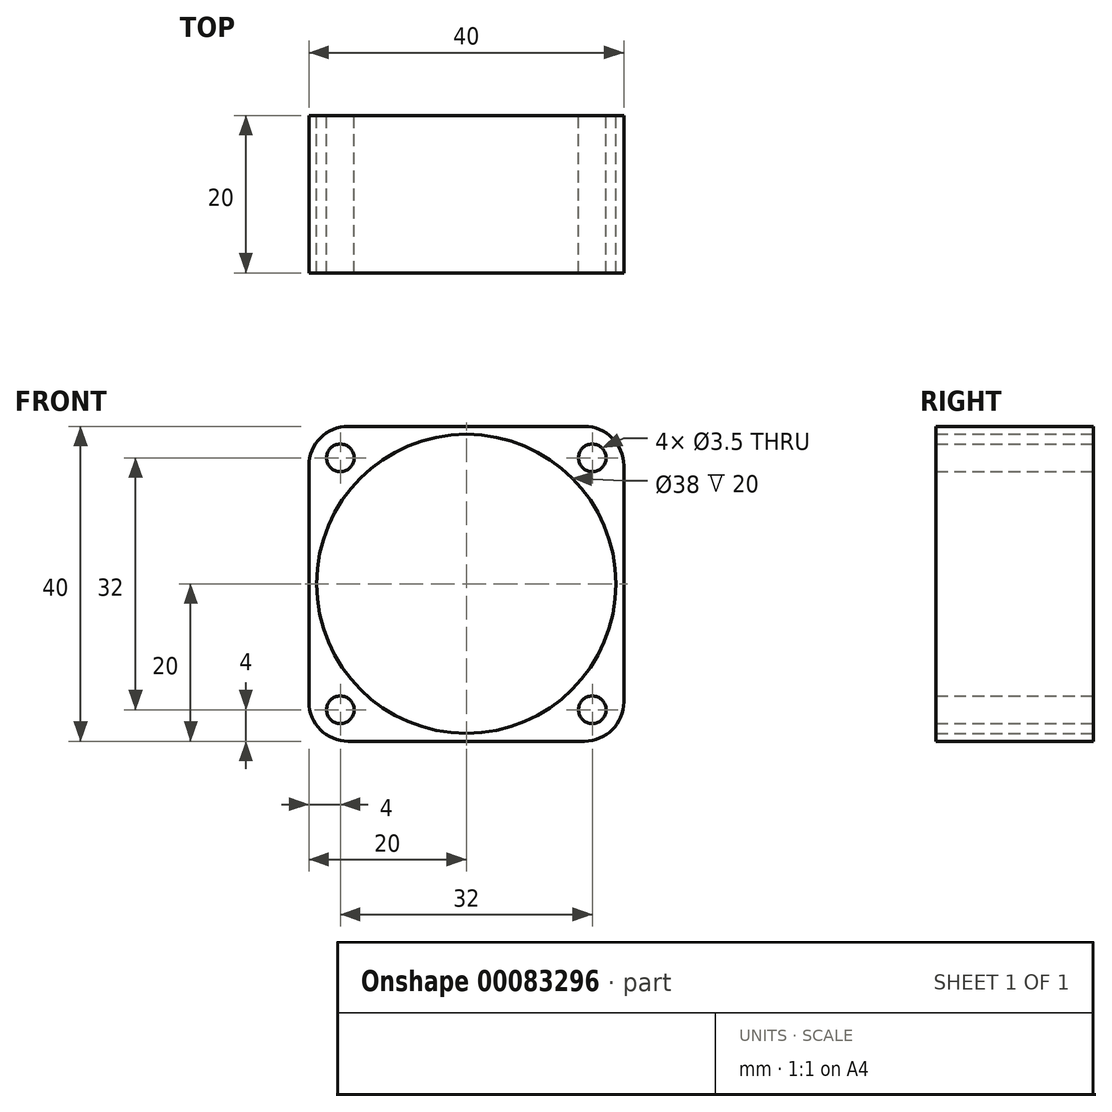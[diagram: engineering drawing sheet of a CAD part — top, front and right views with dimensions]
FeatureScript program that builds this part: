
annotation { "Feature Type Name" : "Feature", "Feature Type Description" : "" }
export const myFeature = defineFeature(function(context is Context, id is Id, definition is map)
    precondition{}
    {
        {
            var Q0;
            Q0=qCreatedBy(makeId("Front.planeOp"),FACE);
            var sketch = newSketch(context, id + "F0", { "sketchPlane" : qUnion([Q0])});
            skLineSegment(sketch, "E0.bottom", {"start": v(20, 20) * mm, "end": v(-20, 20) * mm});
            skLineSegment(sketch, "E0.top", {"start": v(20, -20) * mm, "end": v(-20, -20) * mm});
            skLineSegment(sketch, "E0.left", {"start": v(20, 20) * mm, "end": v(20, -20) * mm});
            skLineSegment(sketch, "E0.right", {"start": v(-20, 20) * mm, "end": v(-20, -20) * mm});
            skPoint(sketch, "E0.middle", {"position": v(0, 0) * mm});
            skCircle(sketch, "E1", {"center": v(0, 0) * mm, "radius": 19 * mm});
            skLineSegment(sketch, "E2.bottom", {"start": v(16, 16) * mm, "end": v(-16, 16) * mm, "construction": true});
            skLineSegment(sketch, "E2.top", {"start": v(16, -16) * mm, "end": v(-16, -16) * mm, "construction": true});
            skLineSegment(sketch, "E2.left", {"start": v(16, 16) * mm, "end": v(16, -16) * mm, "construction": true});
            skLineSegment(sketch, "E2.right", {"start": v(-16, 16) * mm, "end": v(-16, -16) * mm, "construction": true});
            skCircle(sketch, "E3", {"center": v(-16, -16) * mm, "radius": 1.75 * mm});
            skCircle(sketch, "E4", {"center": v(-16, 16) * mm, "radius": 1.75 * mm});
            skCircle(sketch, "E5", {"center": v(16, 16) * mm, "radius": 1.75 * mm});
            skCircle(sketch, "E6", {"center": v(16, -16) * mm, "radius": 1.75 * mm});
            skSolve(sketch);
        }
        {
            var Q0;
            Q0 = qSketchRegion(id + "F0", true);
            extrude(context, id + "F1", {"entities" : qUnion([Q0]), "depth" : 20 * mm});
        }
        {
            var Q0;
            Q0=makeQuery(id+"F1.opExtrude","SWEPT_EDGE",EDGE,{"disambiguationData":[OSD([sQuery(id+"F0.wireOp",EDGE,"E0.bottom"),sQuery(id+"F0.wireOp",EDGE,"E0.right")])]});
            var Q1;
            Q1=makeQuery(id+"F1.opExtrude","SWEPT_EDGE",EDGE,{"disambiguationData":[OSD([sQuery(id+"F0.wireOp",EDGE,"E0.bottom"),sQuery(id+"F0.wireOp",EDGE,"E0.left")])]});
            var Q2;
            Q2=makeQuery(id+"F1.opExtrude","SWEPT_EDGE",EDGE,{"disambiguationData":[OSD([sQuery(id+"F0.wireOp",EDGE,"E0.top"),sQuery(id+"F0.wireOp",EDGE,"E0.left")])]});
            var Q3;
            Q3=makeQuery(id+"F1.opExtrude","SWEPT_EDGE",EDGE,{"disambiguationData":[OSD([sQuery(id+"F0.wireOp",EDGE,"E0.top"),sQuery(id+"F0.wireOp",EDGE,"E0.right")])]});
            fillet(context, id + "F2", {"entities" : qUnion([Q0, Q1, Q2, Q3]), "radius" : 5 * mm, "tangentPropagation" : true, "allowEdgeOverflow" : false});
        }
    });
